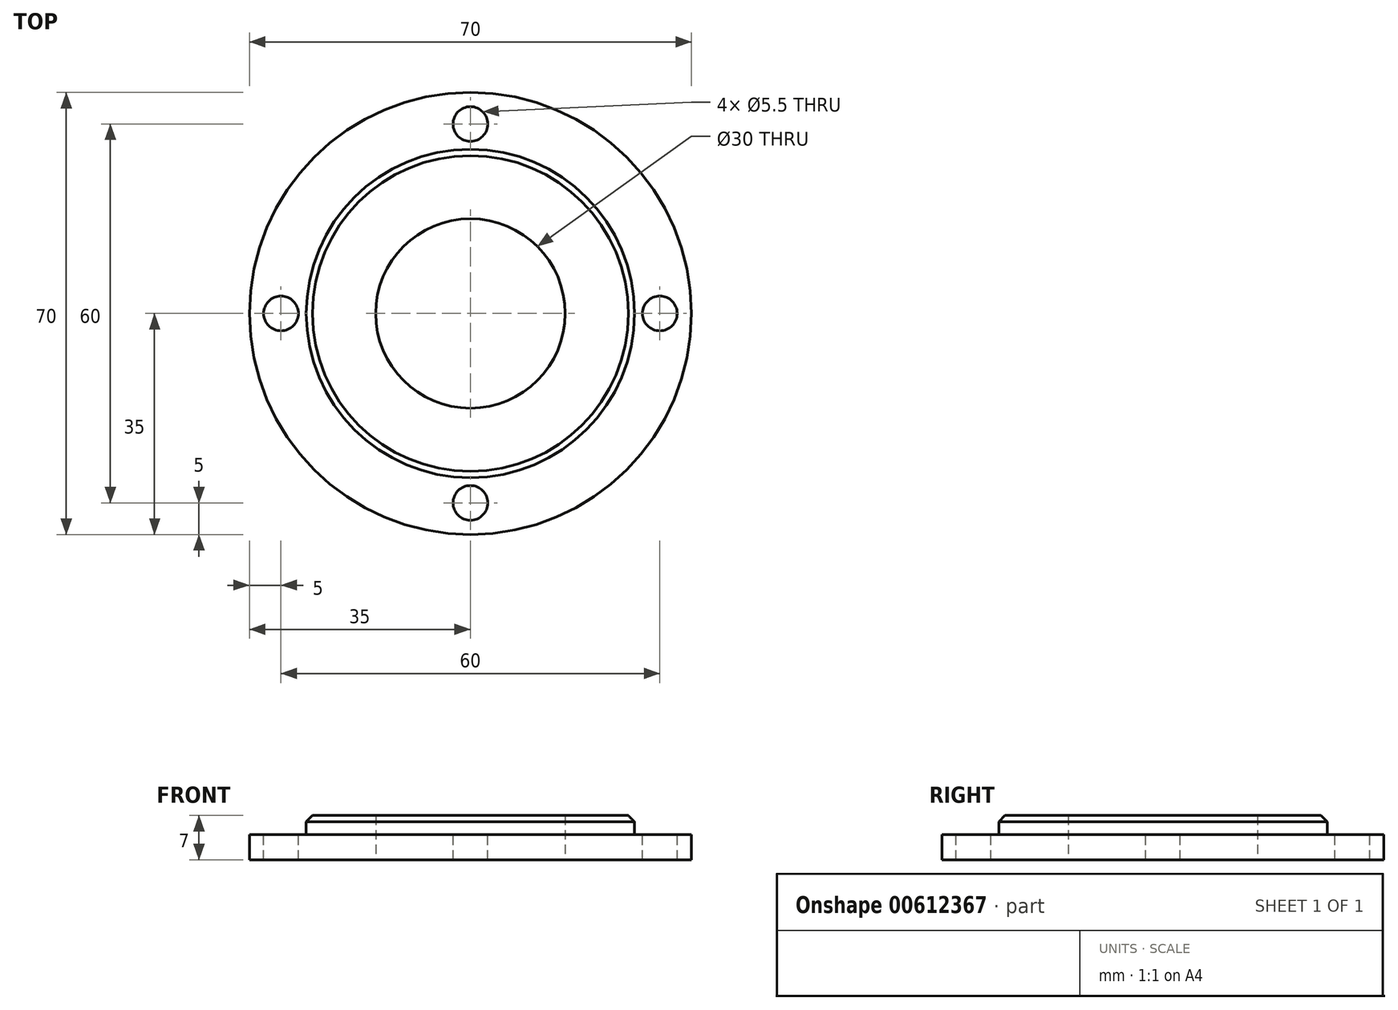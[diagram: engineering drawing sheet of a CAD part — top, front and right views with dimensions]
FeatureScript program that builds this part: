
annotation { "Feature Type Name" : "Feature", "Feature Type Description" : "" }
export const myFeature = defineFeature(function(context is Context, id is Id, definition is map)
    precondition{}
    {
        {
            var Q0;
            Q0=qCreatedBy(makeId("Front.planeOp"),FACE);
            var sketch = newSketch(context, id + "F0", { "sketchPlane" : qUnion([Q0])});
            skLineSegment(sketch, "E0", {"start": v(0, 0) * mm, "end": v(0, 53.65) * mm});
            skLineSegment(sketch, "E1", {"start": v(15, 0) * mm, "end": v(35, 0) * mm});
            skLineSegment(sketch, "E2", {"start": v(35, 0) * mm, "end": v(35, 4) * mm});
            skLineSegment(sketch, "E3", {"start": v(35, 4) * mm, "end": v(26, 4) * mm});
            skLineSegment(sketch, "E4", {"start": v(26, 4) * mm, "end": v(26, 7) * mm});
            skLineSegment(sketch, "E5", {"start": v(26, 7) * mm, "end": v(15, 7) * mm});
            skLineSegment(sketch, "E6", {"start": v(15, 7) * mm, "end": v(15, 0) * mm});
            skSolve(sketch);
        }
        {
            var Q0;
            Q0=makeQuery(id+"F0.imprint","IMPRINT",FACE,{"disambiguationData":[TD([[makeQuery(id+"F0.imprint","IMPRINT",EDGE,{"derivedFrom":sQuery(id+"F0.wireOp",EDGE,"E1")}),1.0]])]});
            var Q1;
            Q1=sQuery(id+"F0.wireOp",EDGE,"E0");
            revolve(context, id + "F1", {"entities" : qUnion([Q0]), "axis" : qUnion([Q1]), "revolveType" : RevolveType.FULL});
        }
        {
            var Q0;
            Q0=makeQuery(id+"F1.opRevolve","SWEPT_EDGE",EDGE,{"disambiguationData":[OSD([sQuery(id+"F0.wireOp",EDGE,"E4"),sQuery(id+"F0.wireOp",EDGE,"E5")])]});
            chamfer(context, id + "F2", {"entities" : qUnion([Q0]), "width" : 1 * mm, "tangentPropagation" : true});
        }
        {
            var Q0;
            Q0=makeQuery(id+"F1.opRevolve","SWEPT_FACE",FACE,{"disambiguationData":[OSD([sQuery(id+"F0.wireOp",EDGE,"E3")])]});
            var sketch = newSketch(context, id + "F3", { "sketchPlane" : qUnion([Q0])});
            skArc(sketch, "E7", {"start": v(-2.75, 29.87) * mm, "mid": v(-21.21, 21.21) * mm, "end": v(-29.87, 2.75) * mm});
            skCircle(sketch, "E8", {"center": v(30, 0) * mm, "radius": 2.75 * mm});
            skCircle(sketch, "E9.1.0", {"center": v(0, 30) * mm, "radius": 2.75 * mm});
            skCircle(sketch, "E9.2.0", {"center": v(-30, 0) * mm, "radius": 2.75 * mm});
            skCircle(sketch, "E9.3.0", {"center": v(0, -30) * mm, "radius": 2.75 * mm});
            skArc(sketch, "E10.trimOffspring", {"start": v(-29.87, -2.75) * mm, "mid": v(-21.21, -21.21) * mm, "end": v(-2.75, -29.87) * mm});
            skArc(sketch, "E11.trimOffspring", {"start": v(2.75, -29.87) * mm, "mid": v(21.21, -21.21) * mm, "end": v(29.87, -2.75) * mm});
            skArc(sketch, "E12.trimOffspring", {"start": v(29.87, 2.75) * mm, "mid": v(21.21, 21.21) * mm, "end": v(2.75, 29.87) * mm});
            skSolve(sketch);
        }
        {
            var Q0;
            {var subQ0=sQuery(id+"F3.wireOp",EDGE,"E9.1.0");var subQ1=makeQuery(id+"F3.imprint","INTERSECT",VERTEX,{"derivedFrom":[sQuery(id+"F3.wireOp",EDGE,"E7"),subQ0]});Q0=makeQuery(id+"F3.imprint","IMPRINT",FACE,{"disambiguationData":[TD([[makeQuery(id+"F3.imprint","IMPRINT",EDGE,{"disambiguationData":[TD([[subQ1,-1.0]])],"derivedFrom":subQ0}),1.0]])]});}
            var Q1;
            {var subQ0=sQuery(id+"F3.wireOp",EDGE,"E9.2.0");var subQ1=makeQuery(id+"F3.imprint","INTERSECT",VERTEX,{"derivedFrom":[sQuery(id+"F3.wireOp",EDGE,"E7"),subQ0]});Q1=makeQuery(id+"F3.imprint","IMPRINT",FACE,{"disambiguationData":[TD([[makeQuery(id+"F3.imprint","IMPRINT",EDGE,{"disambiguationData":[TD([[subQ1,1.0]])],"derivedFrom":subQ0}),1.0]])]});}
            var Q2;
            {var subQ0=sQuery(id+"F3.wireOp",EDGE,"E9.3.0");var subQ1=makeQuery(id+"F3.imprint","INTERSECT",VERTEX,{"derivedFrom":[subQ0,sQuery(id+"F3.wireOp",EDGE,"E10.trimOffspring")]});Q2=makeQuery(id+"F3.imprint","IMPRINT",FACE,{"disambiguationData":[TD([[makeQuery(id+"F3.imprint","IMPRINT",EDGE,{"disambiguationData":[TD([[subQ1,1.0]])],"derivedFrom":subQ0}),1.0]])]});}
            var Q3;
            {var subQ0=sQuery(id+"F3.wireOp",EDGE,"E8");var subQ1=makeQuery(id+"F3.imprint","INTERSECT",VERTEX,{"derivedFrom":[subQ0,sQuery(id+"F3.wireOp",EDGE,"E11.trimOffspring")]});Q3=makeQuery(id+"F3.imprint","IMPRINT",FACE,{"disambiguationData":[TD([[makeQuery(id+"F3.imprint","IMPRINT",EDGE,{"disambiguationData":[TD([[subQ1,1.0]])],"derivedFrom":subQ0}),1.0]])]});}
            extrude(context, id + "F4", {"entities" : qUnion([Q0, Q1, Q2, Q3]), "operationType" : NewBodyOperationType.REMOVE, "oppositeDirection" : true, "depth" : 4 * mm, "offsetDistance" : 25 * mm});
        }
    });
